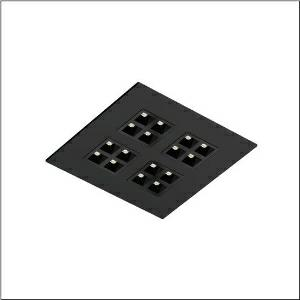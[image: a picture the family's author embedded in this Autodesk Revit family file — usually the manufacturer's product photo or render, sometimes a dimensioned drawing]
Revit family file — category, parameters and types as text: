
# Revit family: silica_r__31_square_51my6lmu34ba_84fe
name_source: partatom
category: Lighting Fixtures
units: mm (PartAtom-declared; Revit-internal decimal feet)

## family parameters
Cut with Voids When Loaded = No
Host = Face
Light Source = No
Part Type = Normal
Room Calculation Point = No
Round Connector Dimension = Use Diameter
Shared = No

## types (1)
- --- (1 x LED, 6250 lm, 39 W, 3000K)
    Apparent Load = 39 VA
    CIE Flux Codes = 82 100 100 100 100
    Color Rendering = 80
    Color Temperature = 3000K
    Default Elevation = 1800 mm
    Description = Silica® 31 Square, office luminaire, primary light control with lens, of PMMA, primary anti-glare with reflector, of PC, black, light emission: direct distribution, primary light characteristic: symmetric, installation type: lay-in mounting, LED, rated luminous flux: 4.600lm, luminous efficacy: 166lm/W, light colour: 830, colour temperature: 3000K, control gear: ON/OFF Multilumen, with terminal, 3-pole, mains connection: 220..240V, AC, 50/60Hz, rated input power: 27.7W, luminaire housing, of sheet steel, coated, jet black (RAL 9005), module: M625, length: 620mm, width: 620mm, height: 43mm, protection rating (complete): IP20, insulation class (complete): insulation class I (protective earthing), certification: CE, impact resistance: IK03, permissible operating ambient temperature: -20..+35°C, standard: EN 50419, packaging unit: 1 piece
    Height = 0 mm  [stored 0 ft]
    Lamp = 1 x LED
    Lamp Light Flux = 6250 lm
    Lamp Power = 39 W
    Lamp count = 1
    Length = 620 mm
    Luminous efficacy = 160 lm/W
    Manufacturer = Siteco
    ModVariant = No
    Model = 51MY6LMU34BA
    Mounting Place = Ceiling
    Mounting Type = Recessed
    Number of Poles = 1
    OnlyDefault = Yes
    Power Factor = 1
    Product Name = Silica® 31 Square
    Product group = office luminaire | ceiling recessed
    ProductGroupID = 400
    Protection Class = Protection class I
    Protection Degree = IP 20
    RLX_Detail_Level = 1
    RLX_Emergency_Light_Flux = 0 lm
    RLX_Emergency_Type = 0
    RLX_Emergency_Type_DB = No
    RlxData = <blob elided: 29001 chars, md5=5384cc6c>
    Socket = socket
    Standby Power = 0 W
    System Light Flux = 6250 lm
    System Power = 39 W
    Type Comments = factory setting: luminous flux: 100 % | (ON | ON | ON | ON) | 1100 mA
    Type Image = l_1313660.jpg
    URL = http://relux.com
    VarID = @adj_033050
    Voltage = 0 V
    Weight = 0.00 kg
    Width = 620 mm

note: [stored X ft] marks values corroborated as IEEE doubles in the binary element streams (Revit-internal decimal feet)

## geometry (parser evidence)
native form markers: Blend x4, Sweep x9
no freeform markers — native parametric forms only
